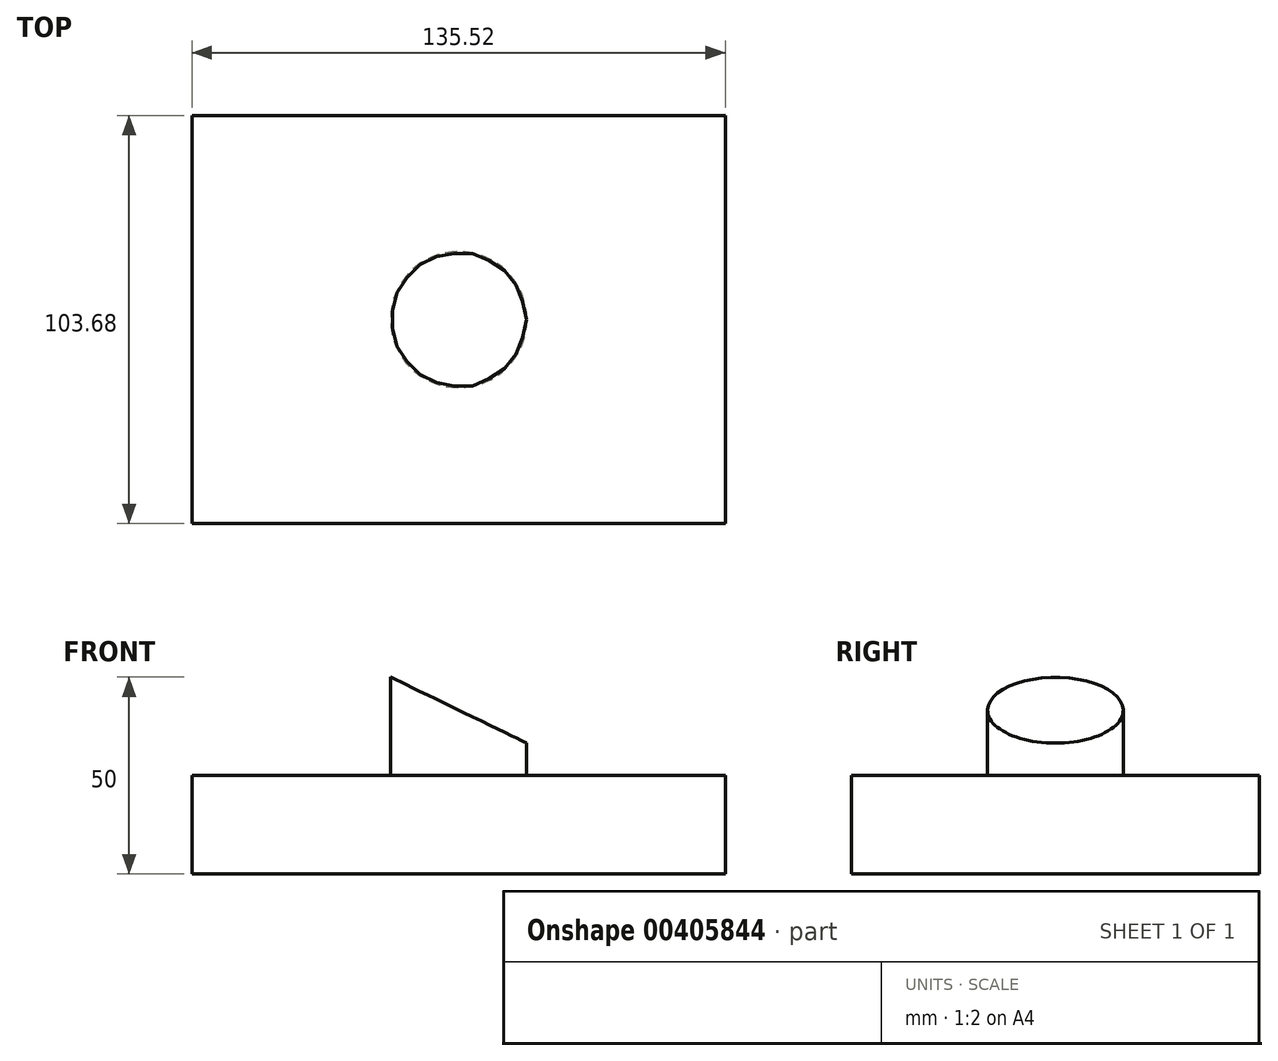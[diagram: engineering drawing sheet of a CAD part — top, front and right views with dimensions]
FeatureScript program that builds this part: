
annotation { "Feature Type Name" : "Feature", "Feature Type Description" : "" }
export const myFeature = defineFeature(function(context is Context, id is Id, definition is map)
    precondition{}
    {
        {
            var Q0;
            Q0=qCreatedBy(makeId("Top.planeOp"),FACE);
            var sketch = newSketch(context, id + "F0", { "sketchPlane" : qUnion([Q0])});
            skLineSegment(sketch, "E0.bottom", {"start": v(-67.76, 51.84) * mm, "end": v(67.76, 51.84) * mm});
            skLineSegment(sketch, "E0.top", {"start": v(-67.76, -51.84) * mm, "end": v(67.76, -51.84) * mm});
            skLineSegment(sketch, "E0.left", {"start": v(-67.76, 51.84) * mm, "end": v(-67.76, -51.84) * mm});
            skLineSegment(sketch, "E0.right", {"start": v(67.76, 51.84) * mm, "end": v(67.76, -51.84) * mm});
            skPoint(sketch, "E0.middle", {"position": v(0, 0) * mm});
            skSolve(sketch);
        }
        {
            var Q0;
            Q0=makeQuery(id+"F0.imprint","IMPRINT",FACE,{"disambiguationData":[TD([[makeQuery(id+"F0.imprint","IMPRINT",EDGE,{"derivedFrom":sQuery(id+"F0.wireOp",EDGE,"E0.bottom")}),-1.0]])]});
            extrude(context, id + "F1", {"entities" : qUnion([Q0]), "depth" : 25 * mm});
        }
        {
            var Q0;
            Q0=makeQuery(id+"F1.opExtrude","CAP_FACE",FACE,{"disambiguationData":[OSD([sQuery(id+"F0.wireOp",EDGE,"E0.bottom"),sQuery(id+"F0.wireOp",EDGE,"E0.top"),sQuery(id+"F0.wireOp",EDGE,"E0.left"),sQuery(id+"F0.wireOp",EDGE,"E0.right")])],"isStart":false});
            var sketch = newSketch(context, id + "F2", { "sketchPlane" : qUnion([Q0])});
            skCircle(sketch, "E1", {"center": v(0, 0) * mm, "radius": 17.27 * mm});
            skSolve(sketch);
        }
        {
            var Q0;
            Q0=makeQuery(id+"F2.imprint","IMPRINT",FACE,{"disambiguationData":[TD([[makeQuery(id+"F2.imprint","IMPRINT",EDGE,{"derivedFrom":sQuery(id+"F2.wireOp",EDGE,"E1")}),1.0]])]});
            var Q1;
            Q1 = qSketchRegion(id + "F4", true);
            extrude(context, id + "F3", {"entities" : qUnion([Q0, Q1]), "operationType" : NewBodyOperationType.ADD, "depth" : 25 * mm});
        }
        {
            var Q0;
            Q0=makeQuery(id+"F1.opExtrude","SWEPT_FACE",FACE,{"disambiguationData":[OSD([sQuery(id+"F0.wireOp",EDGE,"E0.top")])]});
            var sketch = newSketch(context, id + "F4", { "sketchPlane" : qUnion([Q0])});
            skLineSegment(sketch, "E2", {"start": v(-17.27, 25) * mm, "end": v(-17.27, 50) * mm});
            skLineSegment(sketch, "E3", {"start": v(17.27, 50) * mm, "end": v(17.27, 25) * mm});
            skLineSegment(sketch, "E4", {"start": v(-17.27, 50) * mm, "end": v(23.76, 30.08) * mm});
            skLineSegment(sketch, "E5", {"start": v(23.76, 30.08) * mm, "end": v(23.76, 58.12) * mm});
            skLineSegment(sketch, "E6", {"start": v(23.76, 58.12) * mm, "end": v(-17.27, 50) * mm});
            skSolve(sketch);
        }
        {
            var Q0;
            {var subQ3=sQuery(id+"F4.wireOp",EDGE,"E5");Q0=makeQuery(id+"F4.imprint","IMPRINT",FACE,{"disambiguationData":[TD([[makeQuery(id+"F4.imprint","IMPRINT",EDGE,{"derivedFrom":subQ3}),1.0]])]});}
            extrude(context, id + "F5", {"entities" : qUnion([Q0]), "operationType" : NewBodyOperationType.REMOVE, "endBound" : BoundingType.THROUGH_ALL, "oppositeDirection" : true, "depth" : 25 * mm});
        }
    });
